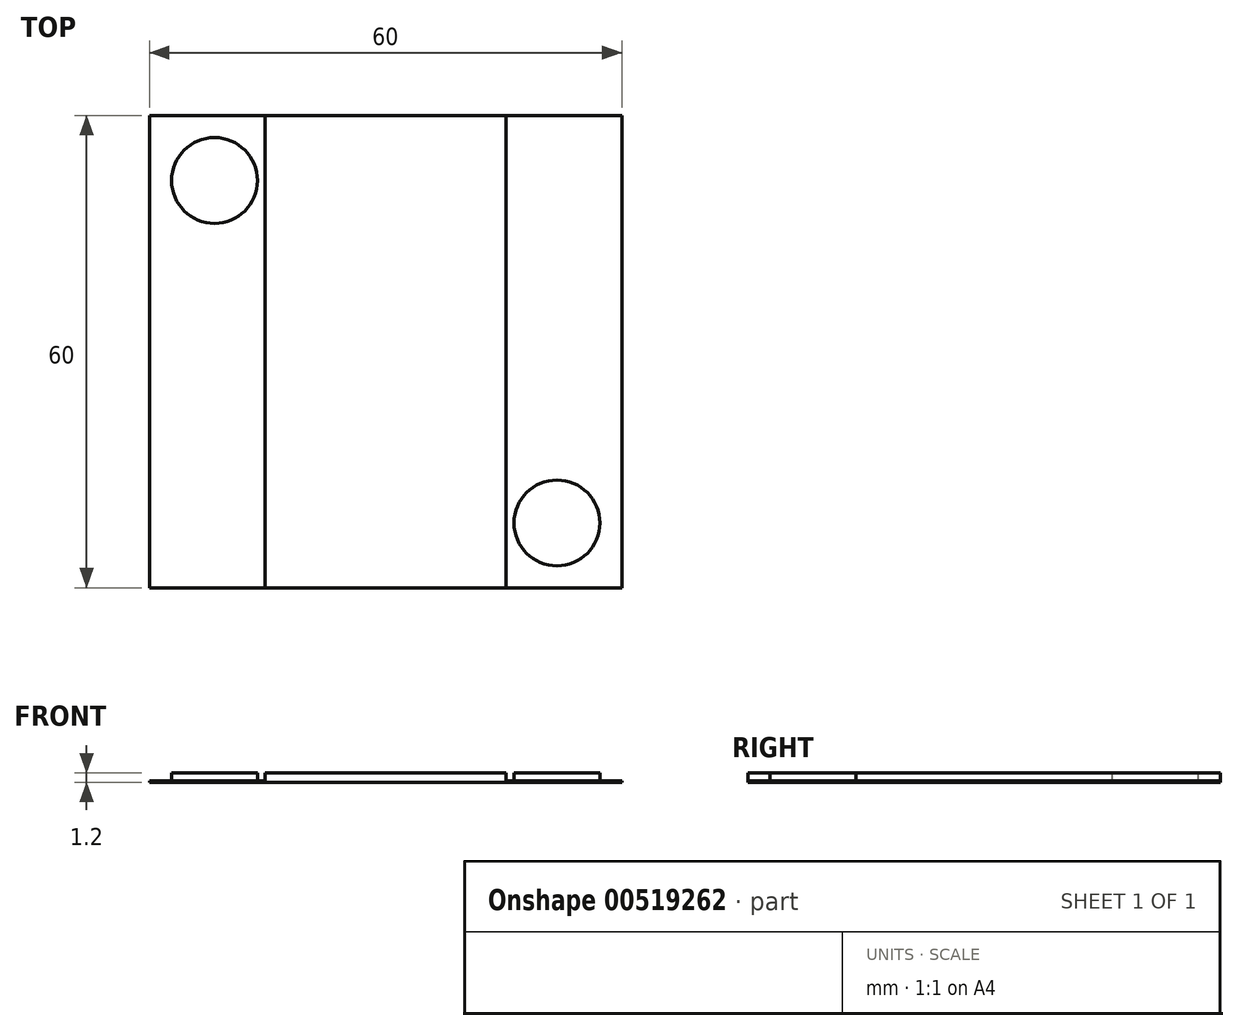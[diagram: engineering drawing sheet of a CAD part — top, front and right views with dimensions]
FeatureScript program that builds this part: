
annotation { "Feature Type Name" : "Feature", "Feature Type Description" : "" }
export const myFeature = defineFeature(function(context is Context, id is Id, definition is map)
    precondition{}
    {
        {
            var Q0;
            Q0=qCreatedBy(makeId("Top.planeOp"),FACE);
            var sketch = newSketch(context, id + "F0", { "sketchPlane" : qUnion([Q0])});
            skLineSegment(sketch, "E0.bottom", {"start": v(-30, 30) * mm, "end": v(30, 30) * mm});
            skLineSegment(sketch, "E0.top", {"start": v(-30, -30) * mm, "end": v(30, -30) * mm});
            skLineSegment(sketch, "E0.left", {"start": v(-30, 30) * mm, "end": v(-30, -30) * mm});
            skLineSegment(sketch, "E0.right", {"start": v(30, 30) * mm, "end": v(30, -30) * mm});
            skPoint(sketch, "E0.middle", {"position": v(0, 0) * mm});
            skPoint(sketch, "E1.visualSharp", {"position": v(30, 30) * mm});
            skLineSegment(sketch, "E1.filletArc", {"start": v(30, 30) * mm, "end": v(30, 30) * mm});
            skSolve(sketch);
        }
        {
            var Q0;
            Q0=makeQuery(id+"F0.imprint","IMPRINT",FACE,{"disambiguationData":[TD([[makeQuery(id+"F0.imprint","IMPRINT",EDGE,{"derivedFrom":sQuery(id+"F0.wireOp",EDGE,"E0.bottom")}),-1.0]])]});
            extrude(context, id + "F1", {"entities" : qUnion([Q0]), "depth" : 1.2 * mm, "offsetDistance" : 25 * mm});
        }
        {
            var Q0;
            Q0=makeQuery(id+"F1.opExtrude","CAP_FACE",FACE,{"disambiguationData":[OSD([sQuery(id+"F0.wireOp",EDGE,"E0.bottom"),sQuery(id+"F0.wireOp",EDGE,"E0.top"),sQuery(id+"F0.wireOp",EDGE,"E0.left"),sQuery(id+"F0.wireOp",EDGE,"E0.right")])],"isStart":false});
            var sketch = newSketch(context, id + "F2", { "sketchPlane" : qUnion([Q0])});
            skCircle(sketch, "E2", {"center": v(21.75, 21.75) * mm, "radius": 5.45 * mm});
            skCircle(sketch, "E3.MirrorC", {"center": v(-21.75, 21.75) * mm, "radius": 5.45 * mm});
            skCircle(sketch, "E4.MirrorC", {"center": v(-21.75, -21.75) * mm, "radius": 5.45 * mm});
            skCircle(sketch, "E5.MirrorC", {"center": v(21.75, -21.75) * mm, "radius": 5.45 * mm});
            skLineSegment(sketch, "E6", {"start": v(22.75, 30) * mm, "end": v(22.75, -30) * mm});
            skLineSegment(sketch, "E7.MirrorCS", {"start": v(-22.75, 30) * mm, "end": v(-22.75, -30) * mm});
            skLineSegment(sketch, "E8", {"start": v(15.3, 30) * mm, "end": v(15.3, -30) * mm});
            skLineSegment(sketch, "E9.MirrorCS", {"start": v(-15.3, 30) * mm, "end": v(-15.3, -30) * mm});
            skSolve(sketch);
        }
        {
            var Q0;
            Q0=makeQuery(id+"F2.imprint","IMPRINT",FACE,{"disambiguationData":[TD([[makeQuery(id+"F2.imprint","IMPRINT",EDGE,{"derivedFrom":sQuery(id+"F2.wireOp",EDGE,"E3.MirrorC")}),-1.0]])]});
            var Q1;
            Q1=makeQuery(id+"F2.imprint","IMPRINT",FACE,{"disambiguationData":[TD([[makeQuery(id+"F2.imprint","IMPRINT",EDGE,{"derivedFrom":sQuery(id+"F2.wireOp",EDGE,"E2")}),1.0]])]});
            var Q2;
            Q2=makeQuery(id+"F2.imprint","IMPRINT",FACE,{"disambiguationData":[TD([[makeQuery(id+"F2.imprint","IMPRINT",EDGE,{"derivedFrom":sQuery(id+"F2.wireOp",EDGE,"E5.MirrorC")}),-1.0]])]});
            var Q3;
            Q3=makeQuery(id+"F2.imprint","IMPRINT",FACE,{"disambiguationData":[TD([[makeQuery(id+"F2.imprint","IMPRINT",EDGE,{"derivedFrom":sQuery(id+"F2.wireOp",EDGE,"E4.MirrorC")}),1.0]])]});
            extrude(context, id + "F3", {"entities" : qUnion([Q0, Q1, Q2, Q3]), "operationType" : NewBodyOperationType.REMOVE, "oppositeDirection" : true, "depth" : 1 * mm, "offsetDistance" : 25 * mm});
        }
    });
